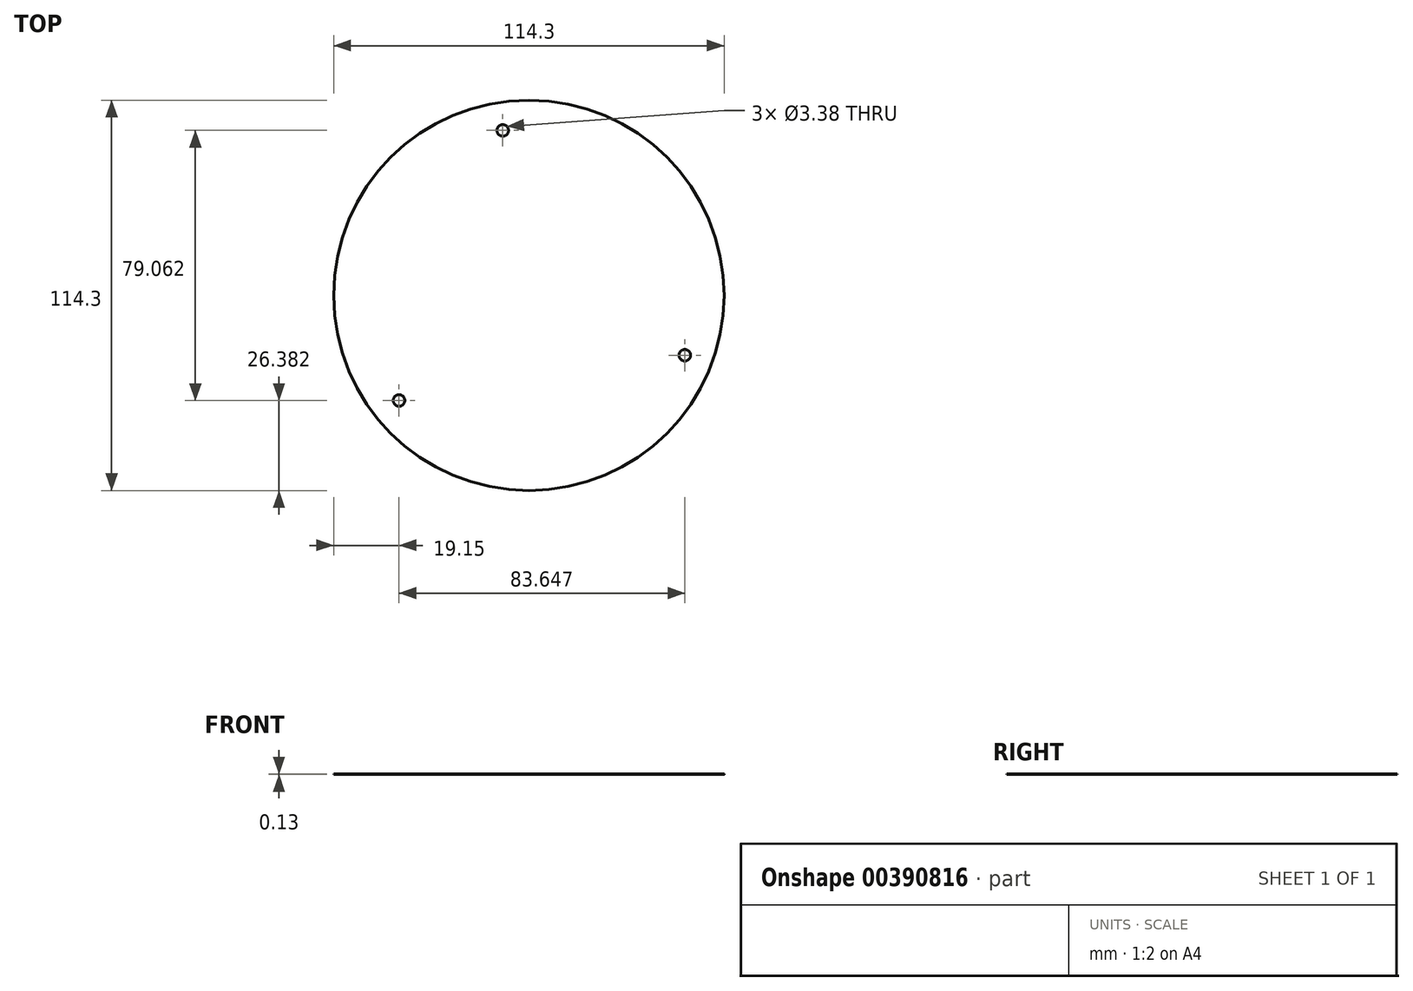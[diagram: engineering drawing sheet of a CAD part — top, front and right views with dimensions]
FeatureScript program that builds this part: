
annotation { "Feature Type Name" : "Feature", "Feature Type Description" : "" }
export const myFeature = defineFeature(function(context is Context, id is Id, definition is map)
    precondition{}
    {
        {
            var Q0;
            Q0=qCreatedBy(makeId("Top.planeOp"),FACE);
            var sketch = newSketch(context, id + "F0", { "sketchPlane" : qUnion([Q0])});
            skCircle(sketch, "E0", {"center": v(0, 0) * mm, "radius": 57.15 * mm});
            skLineSegment(sketch, "E1", {"start": v(-31.75, -43.27) * mm, "end": v(31.75, -43.27) * mm});
            skLineSegment(sketch, "E2", {"start": v(0, 119.3) * mm, "end": v(0, -94.54) * mm, "construction": true});
            skArc(sketch, "E3", {"start": v(31.75, -43.27) * mm, "mid": v(0, -11.52) * mm, "end": v(-31.75, -43.27) * mm});
            skCircle(sketch, "E4", {"center": v(-7.65, 48.3) * mm, "radius": 1.69 * mm});
            skCircle(sketch, "E5.1.0", {"center": v(-38, -30.77) * mm, "radius": 1.69 * mm});
            skCircle(sketch, "E5.2.0", {"center": v(45.65, -17.53) * mm, "radius": 1.69 * mm});
            skCircle(sketch, "E6", {"center": v(0, 0) * mm, "radius": 48.9 * mm, "construction": true});
            skSolve(sketch);
        }
        {
            var Q0;
            Q0 = qSketchRegion(id + "F0", true);
            var Q1;
            Q1=makeQuery(id+"F0.imprint","IMPRINT",FACE,{"disambiguationData":[TD([[makeQuery(id+"F0.imprint","IMPRINT",EDGE,{"derivedFrom":sQuery(id+"F0.wireOp",EDGE,"E1")}),1.0]])]});
            extrude(context, id + "F1", {"entities" : qUnion([Q0, Q1]), "depth" : 0.13 * mm});
        }
    });
